# Revit family: Haworth_Cappellini_Branch_Table_Square_AP_PRELIMINARY
name_source: partatom
category: Furniture
units: mm (PartAtom-declared; Revit-internal decimal feet)

## family parameters
Always vertical = Yes
Cut with Voids When Loaded = No
OmniClass Number = 23.40.70.14.64.21
OmniClass Title = Systems Furniture
Room Calculation Point = No
Shared = No
Work Plane-Based = No

## types (1)
- Square
    Actual Depth = 1500 mm  [stored 4.92126 ft]
    Actual Height = 730 mm  [stored 2.39501 ft]
    Actual Width = 1500 mm  [stored 4.92126 ft]
    Assembly Code = E2020200
    Description = Haworth - Cappellini - Branch - Table - 1500w
    Manufacturer = Haworth
    Model = BR_2XX
    Revision Number = 1
    Size = Verify Final Dim. w/ Haworth
    Table Thickness = 10 mm  [stored 0.0328084 ft]
    URL = https://www.haworth.com
    URL - Product = https://www.haworth.com
    Warranty = http://www.haworth.com

note: [stored X ft] marks values corroborated as IEEE doubles in the binary element streams (Revit-internal decimal feet)

## geometry (parser evidence)
native form markers: Sweep x6
no freeform markers — native parametric forms only
